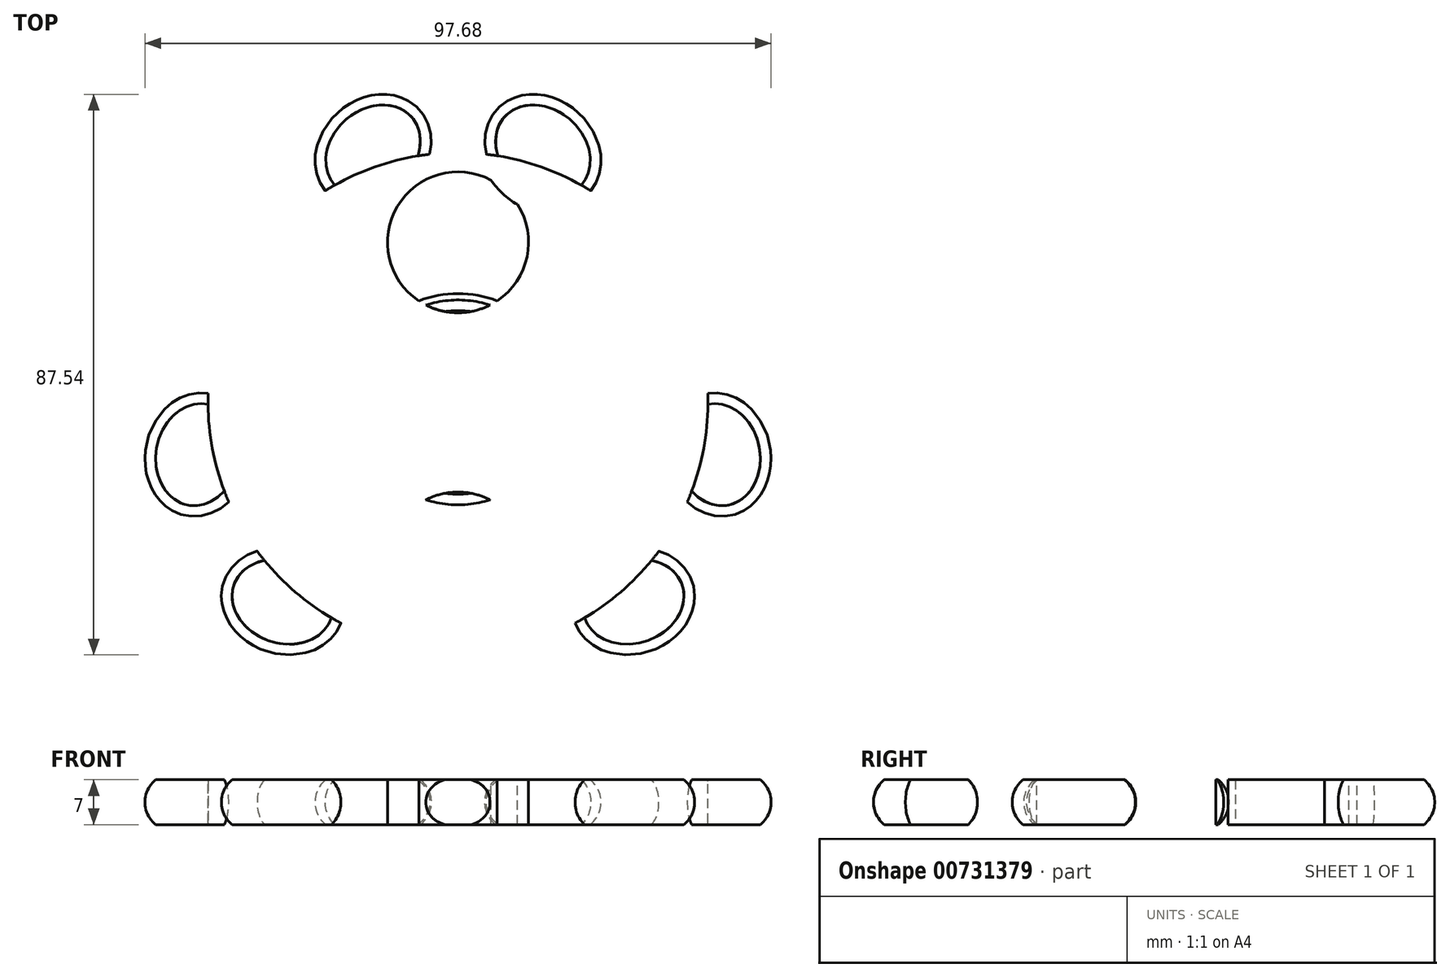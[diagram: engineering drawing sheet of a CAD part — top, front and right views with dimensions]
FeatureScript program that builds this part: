
annotation { "Feature Type Name" : "Feature", "Feature Type Description" : "" }
export const myFeature = defineFeature(function(context is Context, id is Id, definition is map)
    precondition{}
    {
        {
            var Q0;
            Q0=qCreatedBy(makeId("Front.planeOp"),FACE);
            var sketch = newSketch(context, id + "F0", { "sketchPlane" : qUnion([Q0])});
            skLineSegment(sketch, "E0", {"start": v(0, 15.15) * mm, "end": v(0, -20.96) * mm, "construction": true});
            skSolve(sketch);
        }
        {
            var Q0;
            Q0=qCreatedBy(makeId("Top.planeOp"),FACE);
            var sketch = newSketch(context, id + "F1", { "sketchPlane" : qUnion([Q0])});
            skCircle(sketch, "E1", {"center": v(0, 0) * mm, "radius": 39 * mm});
            skCircle(sketch, "E2", {"center": v(0, 0) * mm, "radius": 25 * mm});
            skCircle(sketch, "E3", {"center": v(0, 25) * mm, "radius": 11 * mm});
            skCircle(sketch, "E4", {"center": v(0, 0) * mm, "radius": 11 * mm});
            skCircle(sketch, "E5", {"center": v(0, -25) * mm, "radius": 11 * mm});
            skSolve(sketch);
        }
        {
            var Q0;
            Q0=qCreatedBy(makeId("Top.planeOp"),FACE);
            var sketch = newSketch(context, id + "F2", { "sketchPlane" : qUnion([Q0])});
            skCircle(sketch, "E6", {"center": v(0, 25) * mm, "radius": 14 * mm});
            skSolve(sketch);
        }
        {
            var Q0;
            Q0=qCreatedBy(makeId("Top.planeOp"),FACE);
            var sketch = newSketch(context, id + "F3", { "sketchPlane" : qUnion([Q0])});
            skEllipse(sketch, "E7.MirrorC", {"center": v(13.26, 39.26) * mm, "majorRadius": 9.7 * mm, "minorRadius": 8.15 * mm, "majorAxis": v(-0.75, 0.66)});
            skLineSegment(sketch, "E8", {"start": v(5.97, 45.67) * mm, "end": v(20.54, 32.85) * mm, "construction": true});
            skSolve(sketch);
        }
        {
            var Q0;
            Q0 = qSketchRegion(id + "F2", true);
            extrude(context, id + "F4", {"entities" : qUnion([Q0]), "depth" : 7 * mm, "offsetDistance" : 25 * mm, "symmetric" : true});
        }
        {
            var Q0;
            Q0=qCreatedBy(makeId("Right.planeOp"),FACE);
            var sketch = newSketch(context, id + "F5", { "sketchPlane" : qUnion([Q0])});
            skLineSegment(sketch, "E9", {"start": v(39, 3.5) * mm, "end": v(39, -3.5) * mm, "construction": true});
            skArc(sketch, "E10", {"start": v(37.33, -3.5) * mm, "mid": v(39, 0) * mm, "end": v(37.33, 3.5) * mm});
            skLineSegment(sketch, "E11", {"start": v(37.33, 3.5) * mm, "end": v(40, 3.5) * mm});
            skLineSegment(sketch, "E12", {"start": v(40, 3.5) * mm, "end": v(40, -3.5) * mm});
            skLineSegment(sketch, "E13", {"start": v(40, -3.5) * mm, "end": v(37.33, -3.5) * mm});
            skSolve(sketch);
        }
        {
            var Q0;
            Q0=makeQuery(id+"F5.imprint","IMPRINT",FACE,{"disambiguationData":[TD([[makeQuery(id+"F5.imprint","IMPRINT",EDGE,{"derivedFrom":sQuery(id+"F5.wireOp",EDGE,"E10")}),-1.0]])]});
            var Q1;
            Q1=makeQuery(id+"F4.opExtrude","CAP_EDGE",EDGE,{"disambiguationData":[OSD([sQuery(id+"F2.wireOp",EDGE,"E6")])],"isStart":false});
            sweep(context, id + "F6", {"operationType" : NewBodyOperationType.REMOVE, "profiles" : qUnion([Q0]), "path" : qUnion([Q1])});
        }
        {
            var Q0;
            Q0 = qSketchRegion(id + "F3", true);
            var Q1;
            Q1=makeQuery(id+"F4.opExtrude","CAP_FACE",FACE,{"disambiguationData":[OSD([sQuery(id+"F2.wireOp",EDGE,"E6")])],"isStart":false});
            var Q2;
            Q2=makeQuery(id+"F4.opExtrude","CAP_FACE",FACE,{"disambiguationData":[OSD([sQuery(id+"F2.wireOp",EDGE,"E6")])],"isStart":true});
            extrude(context, id + "F7", {"entities" : qUnion([Q0]), "endBound" : BoundingType.UP_TO_SURFACE, "depth" : 25 * mm, "endBoundEntityFace" : qUnion([Q1]), "offsetDistance" : 25 * mm, "hasSecondDirection" : true, "secondDirectionBound" : BoundingType.UP_TO_SURFACE, "secondDirectionOppositeDirection" : true, "secondDirectionDepth" : 25 * mm, "secondDirectionBoundEntityFace" : qUnion([Q2])});
        }
        {
            var Q0;
            Q0=sQuery(id+"F3.wireOp",EDGE,"E8");
            cPoint(context, id + "F8", {"entities" : qUnion([Q0]), "parameter" : 0.5});
        }
        {
            var Q0;
            Q0 = qCreatedBy(id + "F8" ,VERTEX);
            var Q1;
            Q1=sQuery(id+"F3.wireOp",EDGE,"E8");
            cPlane(context, id + "F9", {"entities" : qUnion([Q0, Q1]), "cplaneType" : CPlaneType.LINE_POINT, "offset" : 25 * mm, "width" : 150 * mm, "height" : 150 * mm});
        }
        {
            var Q0;
            Q0=qCreatedBy(id+"F9.planeOp",FACE);
            var sketch = newSketch(context, id + "F10", { "sketchPlane" : qUnion([Q0])});
            skArc(sketch, "E14", {"start": v(44.71, -3.5) * mm, "mid": v(46.39, 0) * mm, "end": v(44.71, 3.5) * mm});
            skLineSegment(sketch, "E15", {"start": v(46.39, 3.5) * mm, "end": v(46.39, -3.5) * mm, "construction": true});
            skLineSegment(sketch, "E16", {"start": v(44.71, 3.5) * mm, "end": v(47.39, 3.5) * mm});
            skLineSegment(sketch, "E17", {"start": v(47.39, 3.5) * mm, "end": v(47.39, -3.5) * mm});
            skLineSegment(sketch, "E18", {"start": v(47.39, -3.5) * mm, "end": v(44.71, -3.5) * mm});
            skSolve(sketch);
        }
        {
            var Q0;
            Q0=makeQuery(id+"F10.imprint","IMPRINT",FACE,{"disambiguationData":[TD([[makeQuery(id+"F10.imprint","IMPRINT",EDGE,{"derivedFrom":sQuery(id+"F10.wireOp",EDGE,"E14")}),-1.0]])]});
            var Q1;
            Q1=makeQuery(id+"F7.opExtrude","CAP_EDGE",EDGE,{"disambiguationData":[OSD([sQuery(id+"F3.wireOp",EDGE,"E7.MirrorC")])],"isStart":false});
            sweep(context, id + "F11", {"operationType" : NewBodyOperationType.REMOVE, "profiles" : qUnion([Q0]), "path" : qUnion([Q1])});
        }
        {
            var Q0;
            Q0=makeQuery(id+"F7.opExtrude","SWEPT_BODY",BODY,{"disambiguationData":[OSD([sQuery(id+"F3.wireOp",EDGE,"E7.MirrorC")])]});
            var Q1;
            Q1=qCreatedBy(makeId("Right.planeOp"),FACE);
            mirror(context, id + "F12", {"operationType" : NewBodyOperationType.ADD, "entities" : qUnion([Q0]), "mirrorPlane" : qUnion([Q1])});
        }
        {
            var Q0;
            Q0=qCreatedBy(makeId("Top.planeOp"),FACE);
            var sketch = newSketch(context, id + "F13", { "sketchPlane" : qUnion([Q0])});
            skCircle(sketch, "E19", {"center": v(0, 0) * mm, "radius": 16 * mm});
            skSolve(sketch);
        }
        {
            var Q0;
            Q0 = qSketchRegion(id + "F13", true);
            var Q1;
            Q1=makeQuery(id+"F4.opExtrude","CAP_FACE",FACE,{"disambiguationData":[OSD([sQuery(id+"F2.wireOp",EDGE,"E6")])],"isStart":false});
            var Q2;
            Q2=makeQuery(id+"F4.opExtrude","CAP_FACE",FACE,{"disambiguationData":[OSD([sQuery(id+"F2.wireOp",EDGE,"E6")])],"isStart":true});
            extrude(context, id + "F14", {"entities" : qUnion([Q0]), "endBound" : BoundingType.UP_TO_SURFACE, "depth" : 25 * mm, "endBoundEntityFace" : qUnion([Q1]), "offsetDistance" : 25 * mm, "hasSecondDirection" : true, "secondDirectionBound" : BoundingType.UP_TO_SURFACE, "secondDirectionOppositeDirection" : true, "secondDirectionDepth" : 25 * mm, "secondDirectionBoundEntityFace" : qUnion([Q2])});
        }
        {
            var Q0;
            Q0=qCreatedBy(makeId("Right.planeOp"),FACE);
            var sketch = newSketch(context, id + "F15", { "sketchPlane" : qUnion([Q0])});
            skArc(sketch, "E20", {"start": v(14.33, -3.5) * mm, "mid": v(16, 0) * mm, "end": v(14.33, 3.5) * mm});
            skLineSegment(sketch, "E21", {"start": v(16, 3.5) * mm, "end": v(16, -3.5) * mm, "construction": true});
            skLineSegment(sketch, "E22", {"start": v(14.33, 3.5) * mm, "end": v(17, 3.5) * mm});
            skLineSegment(sketch, "E23", {"start": v(14.33, -3.5) * mm, "end": v(17, -3.5) * mm});
            skLineSegment(sketch, "E24", {"start": v(17, -3.5) * mm, "end": v(17, 3.5) * mm});
            skSolve(sketch);
        }
        {
            var Q0;
            Q0=makeQuery(id+"F15.imprint","IMPRINT",FACE,{"disambiguationData":[TD([[makeQuery(id+"F15.imprint","IMPRINT",EDGE,{"derivedFrom":sQuery(id+"F15.wireOp",EDGE,"E20")}),-1.0]])]});
            var Q1;
            Q1=sQuery(id+"F0.wireOp",EDGE,"E0");
            revolve(context, id + "F16", {"operationType" : NewBodyOperationType.REMOVE, "surfaceOperationType" : NewSurfaceOperationType.NEW, "entities" : qUnion([Q0]), "axis" : qUnion([Q1]), "revolveType" : RevolveType.FULL, "oppositeDirection" : true});
        }
        {
            var Q0;
            Q0=makeQuery(id+"F4.opExtrude","SWEPT_BODY",BODY,{"disambiguationData":[OSD([sQuery(id+"F2.wireOp",EDGE,"E6")])]});
            var Q1;
            Q1=sQuery(id+"F0.wireOp",EDGE,"E0");
            circularPattern(context, id + "F17", {"entities" : qUnion([Q0]), "axis" : qUnion([Q1]), "angle" : 360 * degree, "instanceCount" : 3, "equalSpace" : true, "computeTransformsWithoutBuiltin" : true});
        }
        {
            var Q0;
            Q0=makeQuery(id+"F1.imprint","IMPRINT",FACE,{"disambiguationData":[TD([[makeQuery(id+"F1.imprint","IMPRINT",EDGE,{"derivedFrom":sQuery(id+"F1.wireOp",EDGE,"E4")}),1.0]])]});
            extrude(context, id + "F18", {"entities" : qUnion([Q0]), "operationType" : NewBodyOperationType.REMOVE, "endBound" : BoundingType.THROUGH_ALL, "oppositeDirection" : true, "depth" : 25 * mm, "offsetDistance" : 25 * mm, "hasSecondDirection" : true, "secondDirectionBound" : BoundingType.THROUGH_ALL, "secondDirectionOppositeDirection" : false, "secondDirectionDepth" : 25 * mm});
        }
        {
            var Q0;
            {var subQ0=sQuery(id+"F1.wireOp",EDGE,"E3");var subQ1=sQuery(id+"F1.wireOp",EDGE,"E2");var subQ2=makeQuery(id+"F1.imprint","INTERSECT",VERTEX,{"disambiguationData":[OD(0.0)],"derivedFrom":[subQ1,subQ0]});Q0=makeQuery(id+"F1.imprint","IMPRINT",FACE,{"disambiguationData":[TD([[makeQuery(id+"F1.imprint","IMPRINT",EDGE,{"disambiguationData":[TD([[subQ2,1.0]])],"derivedFrom":subQ1}),-1.0]])]});}
            var Q1;
            {var subQ0=sQuery(id+"F1.wireOp",EDGE,"E3");var subQ1=sQuery(id+"F1.wireOp",EDGE,"E2");var subQ2=makeQuery(id+"F1.imprint","INTERSECT",VERTEX,{"disambiguationData":[OD(0.0)],"derivedFrom":[subQ1,subQ0]});Q1=makeQuery(id+"F1.imprint","IMPRINT",FACE,{"disambiguationData":[TD([[makeQuery(id+"F1.imprint","IMPRINT",EDGE,{"disambiguationData":[TD([[subQ2,1.0]])],"derivedFrom":subQ1}),1.0]])]});}
            extrude(context, id + "F19", {"entities" : qUnion([Q0, Q1]), "operationType" : NewBodyOperationType.REMOVE, "endBound" : BoundingType.THROUGH_ALL, "oppositeDirection" : true, "depth" : 25 * mm, "offsetDistance" : 25 * mm, "hasSecondDirection" : true, "secondDirectionBound" : BoundingType.THROUGH_ALL, "secondDirectionOppositeDirection" : false, "secondDirectionDepth" : 25 * mm});
        }
    });
